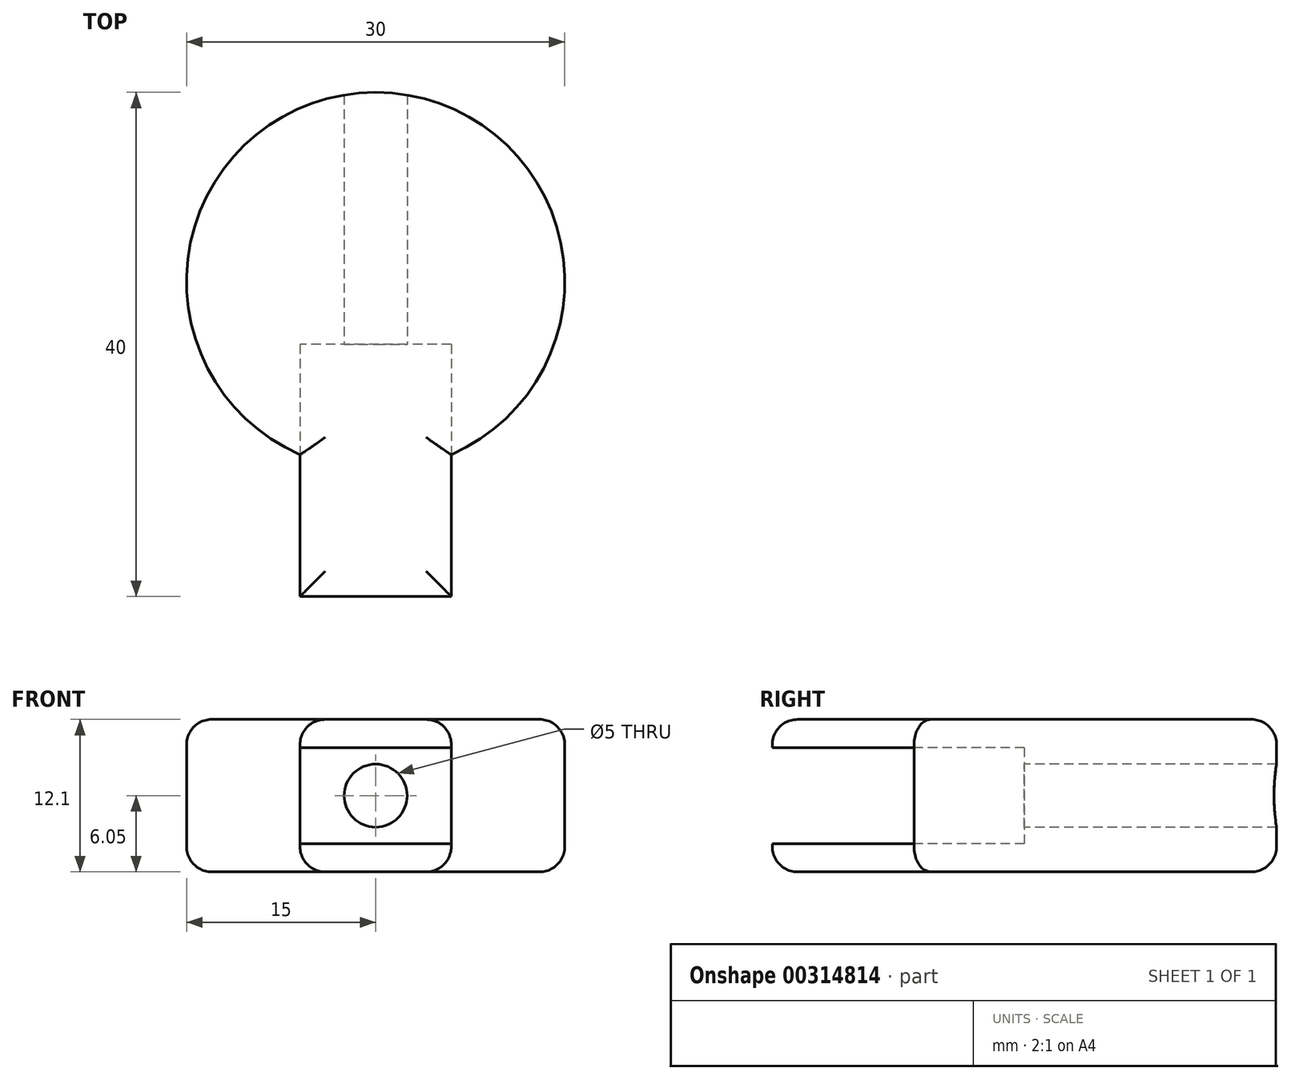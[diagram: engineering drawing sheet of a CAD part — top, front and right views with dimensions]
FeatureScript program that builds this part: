
annotation { "Feature Type Name" : "Feature", "Feature Type Description" : "" }
export const myFeature = defineFeature(function(context is Context, id is Id, definition is map)
    precondition{}
    {
        {
            var Q0;
            Q0=qCreatedBy(makeId("Top.planeOp"),FACE);
            var sketch = newSketch(context, id + "F0", { "sketchPlane" : qUnion([Q0])});
            skArc(sketch, "E0", {"start": v(6, -13.75) * mm, "mid": v(0, 15) * mm, "end": v(-6, -13.75) * mm});
            skLineSegment(sketch, "E1", {"start": v(0, -25) * mm, "end": v(-6, -25) * mm});
            skLineSegment(sketch, "E2", {"start": v(0, -25) * mm, "end": v(6, -25) * mm});
            skLineSegment(sketch, "E3", {"start": v(-6, -25) * mm, "end": v(-6, -13.75) * mm});
            skLineSegment(sketch, "E4", {"start": v(6, -25) * mm, "end": v(6, -13.75) * mm});
            skSolve(sketch);
        }
        {
            var Q0;
            Q0=makeQuery(id+"F0.imprint","IMPRINT",FACE,{"disambiguationData":[TD([[makeQuery(id+"F0.imprint","IMPRINT",EDGE,{"derivedFrom":sQuery(id+"F0.wireOp",EDGE,"E0")}),1.0]])]});
            extrude(context, id + "F1", {"entities" : qUnion([Q0]), "depth" : 12.1 * mm});
        }
        {
            var Q0;
            Q0=makeQuery(id+"F1.opExtrude","CAP_EDGE",EDGE,{"disambiguationData":[OSD([sQuery(id+"F0.wireOp",EDGE,"E0")])],"isStart":false});
            var Q1;
            Q1=makeQuery(id+"F1.opExtrude","CAP_FACE",FACE,{"disambiguationData":[OSD([sQuery(id+"F0.wireOp",EDGE,"E0"),sQuery(id+"F0.wireOp",EDGE,"E1"),sQuery(id+"F0.wireOp",EDGE,"E2"),sQuery(id+"F0.wireOp",EDGE,"E3"),sQuery(id+"F0.wireOp",EDGE,"E4")])],"isStart":false});
            var Q2;
            Q2=makeQuery(id+"F1.opExtrude","CAP_EDGE",EDGE,{"disambiguationData":[OSD([sQuery(id+"F0.wireOp",EDGE,"E0")])],"isStart":true});
            var Q3;
            Q3=makeQuery(id+"F1.opExtrude","CAP_FACE",FACE,{"disambiguationData":[OSD([sQuery(id+"F0.wireOp",EDGE,"E0"),sQuery(id+"F0.wireOp",EDGE,"E1"),sQuery(id+"F0.wireOp",EDGE,"E2"),sQuery(id+"F0.wireOp",EDGE,"E3"),sQuery(id+"F0.wireOp",EDGE,"E4")])],"isStart":true});
            fillet(context, id + "F2", {"entities" : qUnion([Q0, Q1, Q2, Q3]), "radius" : 2 * mm, "tangentPropagation" : true, "allowEdgeOverflow" : false});
        }
        {
            var Q0;
            Q0=makeQuery(id+"F1.opExtrude","SWEPT_FACE",FACE,{"disambiguationData":[OSD([sQuery(id+"F0.wireOp",EDGE,"E1"),sQuery(id+"F0.wireOp",EDGE,"E2")])]});
            var sketch = newSketch(context, id + "F3", { "sketchPlane" : qUnion([Q0])});
            skLineSegment(sketch, "E5.bottom", {"start": v(6, 9.86) * mm, "end": v(-6, 9.86) * mm});
            skLineSegment(sketch, "E5.top", {"start": v(6, 2.24) * mm, "end": v(-6, 2.24) * mm});
            skLineSegment(sketch, "E5.left", {"start": v(6, 9.86) * mm, "end": v(6, 2.24) * mm});
            skLineSegment(sketch, "E5.right", {"start": v(-6, 9.86) * mm, "end": v(-6, 2.24) * mm});
            skPoint(sketch, "E5.middle", {"position": v(0, 6.05) * mm});
            skSolve(sketch);
        }
        {
            var Q0;
            Q0=makeQuery(id+"F3.imprint","IMPRINT",FACE,{"disambiguationData":[TD([[makeQuery(id+"F3.imprint","IMPRINT",EDGE,{"derivedFrom":sQuery(id+"F3.wireOp",EDGE,"E5.bottom")}),1.0]])]});
            extrude(context, id + "F4", {"entities" : qUnion([Q0]), "operationType" : NewBodyOperationType.REMOVE, "oppositeDirection" : true, "depth" : 20 * mm});
        }
        {
            var Q0;
            Q0=makeQuery(id+"F4.boolean.opBoolean","COPY",FACE,{"derivedFrom":makeQuery(id+"F4.opExtrude","CAP_FACE",FACE,{"disambiguationData":[OSD([sQuery(id+"F3.wireOp",EDGE,"E5.bottom"),sQuery(id+"F3.wireOp",EDGE,"E5.top"),sQuery(id+"F3.wireOp",EDGE,"E5.left"),sQuery(id+"F3.wireOp",EDGE,"E5.right")])],"isStart":false})});
            var sketch = newSketch(context, id + "F5", { "sketchPlane" : qUnion([Q0])});
            skLineSegment(sketch, "E6", {"start": v(-6, 9.86) * mm, "end": v(6, 2.24) * mm, "construction": true});
            skLineSegment(sketch, "E7", {"start": v(6, 2.24) * mm, "end": v(6, 9.86) * mm, "construction": true});
            skLineSegment(sketch, "E8", {"start": v(6, 9.86) * mm, "end": v(-6, 2.24) * mm, "construction": true});
            skCircle(sketch, "E9", {"center": v(0, 6.05) * mm, "radius": 2.5 * mm});
            skSolve(sketch);
        }
        {
            var Q0;
            Q0=makeQuery(id+"F5.imprint","IMPRINT",FACE,{"disambiguationData":[TD([[makeQuery(id+"F5.imprint","IMPRINT",EDGE,{"derivedFrom":sQuery(id+"F5.wireOp",EDGE,"E9")}),1.0]])]});
            extrude(context, id + "F6", {"entities" : qUnion([Q0]), "operationType" : NewBodyOperationType.REMOVE, "oppositeDirection" : true, "depth" : 33.78 * mm});
        }
    });
